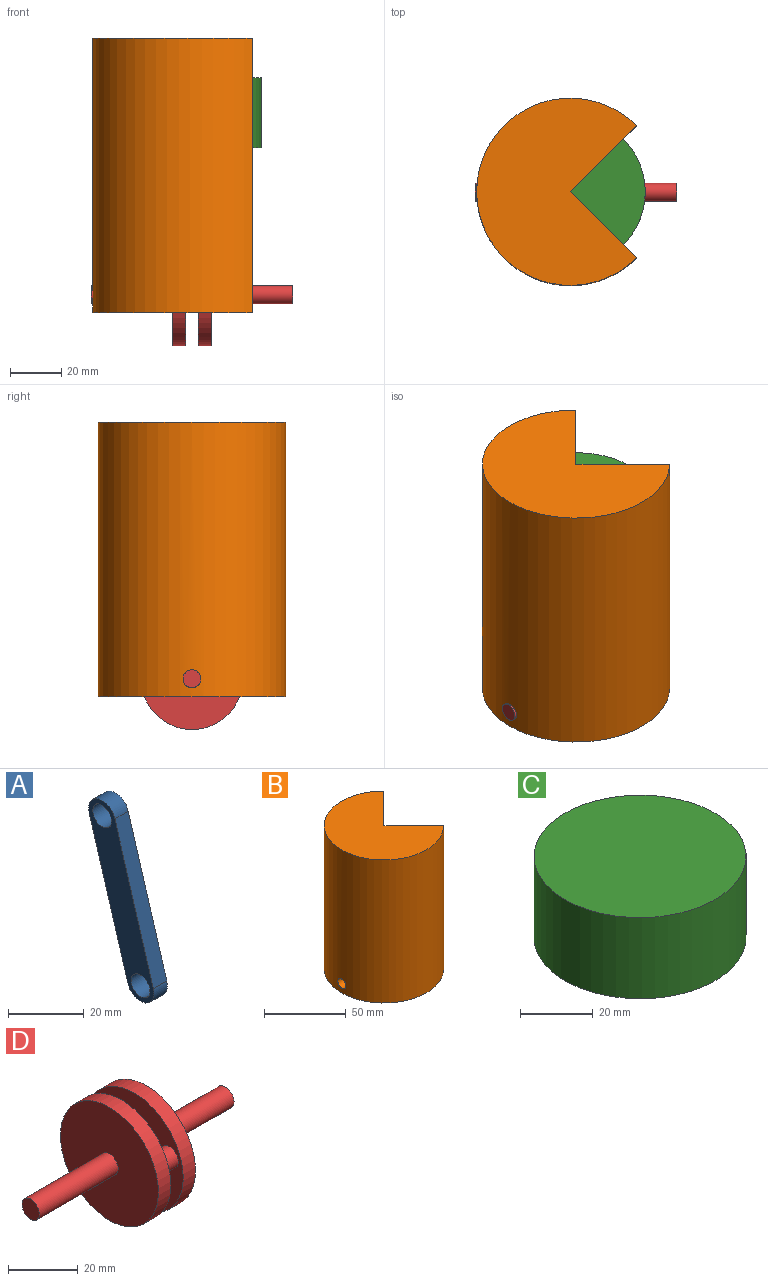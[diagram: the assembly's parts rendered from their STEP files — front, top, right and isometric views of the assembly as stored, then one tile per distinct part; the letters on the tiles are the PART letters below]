
ASSEMBLY  parts=4 mates=4
PART A: 8 faces, bbox 5x24.4x57.9 mm
  f0: cylinder r=5mm len=9.79mm, axis (-1,0,0), area 78.5mm2, adj f1,f3,f6,f7
  f1: plane 47.85x14.4mm, normal (0,0.96,-0.29), area 249.9mm2, adj f0,f2,f6,f7
  f2: cylinder r=5mm len=9.79mm, axis (-1,0,0), area 78.5mm2, adj f1,f3,f6,f7
  f3: plane 47.85x14.4mm, normal (0,-0.96,0.29), area 249.9mm2, adj f0,f2,f6,f7
  f4: cylinder r=3.5mm len=7mm, axis (-1,0,0), area 110mm2, adj f6,f7
  f5: cylinder r=3.5mm len=7mm, axis (-1,0,0), area 110mm2, adj f6,f7
  f6: plane 57.85x24.4mm, normal (1,0,0), area 501.3mm2, adj f0,f1,f2,f3,f4,f5
  f7: plane 57.85x24.4mm, normal (-1,0,0), area 501.3mm2, adj f0,f1,f2,f3,f4,f5
PART B: 8 faces, bbox 62.3x73x107 mm
  f0: plane 73.04x62.35mm, normal (0,0,-1), area 1022.2mm2, adj f1,f4,f5,f6
  f1: cylinder r=30mm len=101mm, axis (0,0,-1), area 14240.1mm2, adj f0,f2,f5,f6,f7
  f2: plane 60x51.21mm, normal (0,0,-1), area 2120.6mm2, adj f1,f5,f6
  f3: plane 73.04x62.35mm, normal (0,0,1), area 3142.8mm2, adj f4,f5,f6
  f4: cylinder r=36.52mm len=107mm, axis (0,0,-1), area 18376.6mm2, adj f0,f3,f5,f6,f7
  f5: plane 107x25.82mm, normal (0.71,0.71,0), area 877.8mm2, adj f0,f1,f2,f3,f4,f6
  f6: plane 107x25.82mm, normal (0.71,-0.71,0), area 877.8mm2, adj f0,f1,f2,f3,f4,f5
  f7: cylinder r=3.5mm len=7mm, axis (1,0,0), area 143.8mm2, adj f1,f4
PART C: 6 faces, bbox 58.5x58.5x27.4 mm
  f0: cylinder r=26.76mm len=53.52mm, axis (0,0,1), area 4109mm2, adj f3,f4,f5
  f1: plane 58.52x58.52mm, normal (0,0,1), area 2689.4mm2, adj f2
  f2: cylinder r=29.26mm len=58.52mm, axis (0,0,1), area 5037mm2, adj f1,f3
  f3: plane 58.52x58.52mm, normal (0,0,-1), area 440mm2, adj f0,f2
  f4: plane 53.52x53.52mm, normal (0,0,-1), area 2249.5mm2, adj f0
  f5: cylinder r=3.5mm len=53.52mm, axis (-1,0,0), area 1171.9mm2, adj f0
PART D: 11 faces, bbox 78.8x39.6x39.6 mm
  f0: cylinder r=3.5mm len=31.9mm, axis (1,0,0), area 701.5mm2, adj f1,f3
  f1: plane 7x7mm, normal (-1,0,0), area 38.5mm2, adj f0
  f2: cylinder r=19.82mm len=39.64mm, axis (1,0,0), area 622.6mm2, adj f3,f4
  f3: plane 39.64x39.64mm, normal (-1,0,0), area 1195.3mm2, adj f0,f2
  f4: plane 39.64x39.64mm, normal (1,0,0), area 1195.3mm2, adj f2,f5
  f5: cylinder r=3.5mm len=7mm, axis (-1,0,0), area 110mm2, adj f4,f10
  f6: cylinder r=3.5mm len=31.9mm, axis (-1,0,0), area 701.5mm2, adj f7,f9
  f7: plane 7x7mm, normal (1,0,0), area 38.5mm2, adj f6
  f8: cylinder r=19.82mm len=39.64mm, axis (-1,0,0), area 622.6mm2, adj f9,f10
  f9: plane 39.64x39.64mm, normal (1,0,0), area 1195.3mm2, adj f6,f8
  f10: plane 39.64x39.64mm, normal (-1,0,0), area 1195.3mm2, adj f5,f8
PLACE A rot(axis=(1,0,0),7.5deg) t=(-38.94,-7.29,27.53)mm
PLACE B t=(-38.69,-14.14,17.45)mm fixed
PLACE C t=(-38.69,-14.14,27.08)mm
PLACE D rot(axis=(-1,0,0),40deg) t=(-38.95,-14.14,17.45)mm
MATE slider C.f0 <-> B.f1  axis (0,0,-1) through (-38.69,-14.14,99.67)mm
MATE cylindrical A.f2 <-> C.f5  axis (-1,0,0) through (-33.94,-14.14,79.6)mm
MATE cylindrical A.f0 <-> D.f5  axis (-1,0,0) through (-33.94,-22.17,30.28)mm
MATE revolute B.f7 <-> D.f0  axis (1,0,0) through (-71.85,-14.14,17.45)mm
